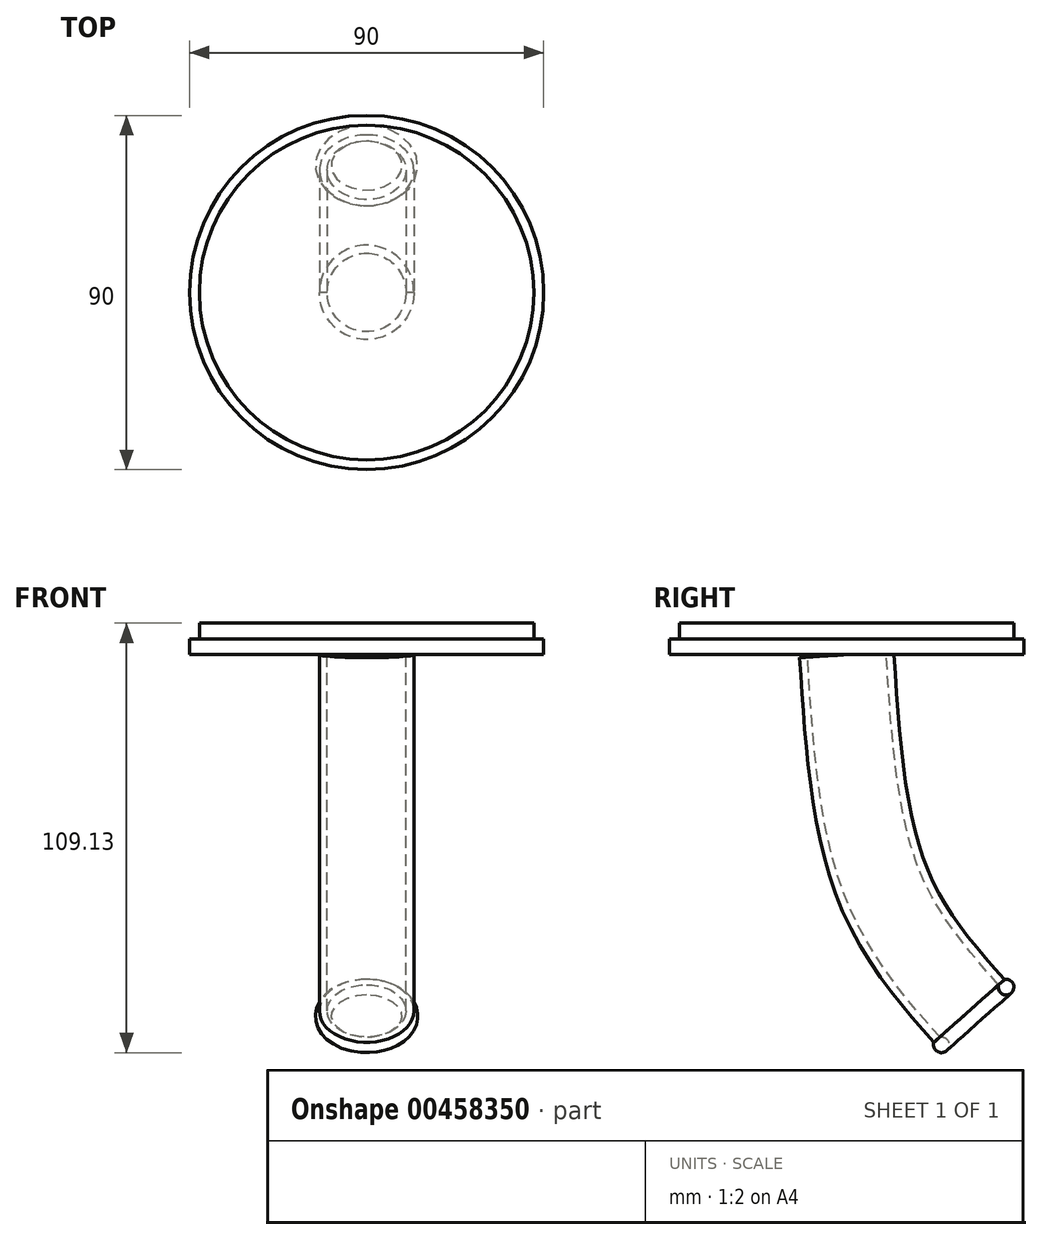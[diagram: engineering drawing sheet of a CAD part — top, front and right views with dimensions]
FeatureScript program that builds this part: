
annotation { "Feature Type Name" : "Feature", "Feature Type Description" : "" }
export const myFeature = defineFeature(function(context is Context, id is Id, definition is map)
    precondition{}
    {
        {
            var Q0;
            Q0=qCreatedBy(makeId("Top.planeOp"),FACE);
            var sketch = newSketch(context, id + "F0", { "sketchPlane" : qUnion([Q0])});
            skCircle(sketch, "E0", {"center": v(0, 0) * mm, "radius": 45 * mm});
            skCircle(sketch, "E1", {"center": v(0, 0) * mm, "radius": 42.5 * mm});
            skSolve(sketch);
        }
        {
            var Q0;
            Q0=makeQuery(id+"F0.imprint","IMPRINT",FACE,{"disambiguationData":[TD([[makeQuery(id+"F0.imprint","IMPRINT",EDGE,{"derivedFrom":sQuery(id+"F0.wireOp",EDGE,"E0")}),1.0]])]});
            extrude(context, id + "F1", {"entities" : qUnion([Q0]), "depth" : 4 * mm});
        }
        {
            var Q0;
            Q0=makeQuery(id+"F0.imprint","IMPRINT",FACE,{"disambiguationData":[TD([[makeQuery(id+"F0.imprint","IMPRINT",EDGE,{"derivedFrom":sQuery(id+"F0.wireOp",EDGE,"E1")}),1.0]])]});
            extrude(context, id + "F2", {"entities" : qUnion([Q0]), "operationType" : NewBodyOperationType.ADD, "depth" : 8 * mm});
        }
        {
            var Q0;
            Q0=qCreatedBy(makeId("Right.planeOp"),FACE);
            var sketch = newSketch(context, id + "F3", { "sketchPlane" : qUnion([Q0])});
            skPoint(sketch, "E2.0", {"position": v(0, 0) * mm});
            skLineSegment(sketch, "E3.0", {"start": v(-45, 0) * mm, "end": v(45, 0) * mm});
            skFitSpline(sketch, "E4", {"points": [v(0, 0) * mm, v(9.12, -58.46) * mm, v(32.23, -91.82) * mm], "startDerivative": vector(7.27, -115.98) * mm, "endDerivative": vector(58.82, -66.1) * mm});
            skSolve(sketch);
        }
        {
            var Q0;
            Q0=sQuery(id+"F3.wireOp",EDGE,"E4");
            var Q1;
            Q1=sQuery(id+"F3.wireOp",VERTEX,"E4.2.internal");
            cPlane(context, id + "F4", {"entities" : qUnion([Q0, Q1]), "cplaneType" : CPlaneType.CURVE_POINT, "offset" : 25.4 * mm, "width" : 152.4 * mm, "height" : 152.4 * mm});
        }
        {
            var Q0;
            Q0=qCreatedBy(id+"F4.planeOp",FACE);
            var sketch = newSketch(context, id + "F5", { "sketchPlane" : qUnion([Q0])});
            skPoint(sketch, "E5.0", {"position": v(0, 36.96) * mm});
            skCircle(sketch, "E6", {"center": v(0, 36.96) * mm, "radius": 10 * mm});
            skCircle(sketch, "E7", {"center": v(0, 36.96) * mm, "radius": 12 * mm});
            skCircle(sketch, "E8", {"center": v(0, 36.96) * mm, "radius": 11 * mm});
            skCircle(sketch, "E9", {"center": v(0, 36.96) * mm, "radius": 13 * mm});
            skPoint(sketch, "E10", {"position": v(2.35, 26.21) * mm});
            skSolve(sketch);
        }
        {
            var Q0;
            Q0=sQuery(id+"F5.wireOp",VERTEX,"E10");
            var Q1;
            Q1=sQuery(id+"F5.wireOp",EDGE,"E8");
            cPlane(context, id + "F6", {"entities" : qUnion([Q0, Q1]), "cplaneType" : CPlaneType.CURVE_POINT, "offset" : 25.4 * mm, "width" : 152.4 * mm, "height" : 152.4 * mm});
        }
        {
            var Q0;
            Q0=qCreatedBy(id+"F6.planeOp",FACE);
            var sketch = newSketch(context, id + "F7", { "sketchPlane" : qUnion([Q0])});
            skPoint(sketch, "E11.0", {"position": v(42.06, -83.45) * mm});
            skLineSegment(sketch, "E12.0", {"start": v(43.54, -82.1) * mm, "end": v(24.32, -99.62) * mm});
            skCircle(sketch, "E13", {"center": v(42.06, -83.45) * mm, "radius": 2 * mm});
            skSolve(sketch);
        }
        {
            var Q0;
            {var subQ0=sQuery(id+"F7.wireOp",EDGE,"E13");var subQ1=sQuery(id+"F7.wireOp",EDGE,"E12.0");var subQ2=makeQuery(id+"F7.imprint","INTERSECT",VERTEX,{"disambiguationData":[OD(0.0)],"derivedFrom":[subQ1,subQ0]});Q0=makeQuery(id+"F7.imprint","IMPRINT",FACE,{"disambiguationData":[TD([[makeQuery(id+"F7.imprint","IMPRINT",EDGE,{"disambiguationData":[TD([[subQ2,-1.0]])],"derivedFrom":subQ1}),1.0]])]});}
            var Q1;
            {var subQ0=sQuery(id+"F7.wireOp",EDGE,"E13");var subQ1=sQuery(id+"F7.wireOp",EDGE,"E12.0");var subQ2=makeQuery(id+"F7.imprint","INTERSECT",VERTEX,{"disambiguationData":[OD(0.0)],"derivedFrom":[subQ1,subQ0]});Q1=makeQuery(id+"F7.imprint","IMPRINT",FACE,{"disambiguationData":[TD([[makeQuery(id+"F7.imprint","IMPRINT",EDGE,{"disambiguationData":[TD([[subQ2,-1.0]])],"derivedFrom":subQ1}),-1.0]])]});}
            var Q2;
            Q2=sQuery(id+"F5.wireOp",EDGE,"E8");
            sweep(context, id + "F8", {"profiles" : qUnion([Q0, Q1]), "path" : qUnion([Q2])});
        }
        {
            var Q0;
            Q0=makeQuery(id+"F5.imprint","IMPRINT",FACE,{"disambiguationData":[TD([[makeQuery(id+"F5.imprint","IMPRINT",EDGE,{"derivedFrom":sQuery(id+"F5.wireOp",EDGE,"E7")}),1.0]])]});
            var Q1;
            Q1=makeQuery(id+"F5.imprint","IMPRINT",FACE,{"disambiguationData":[TD([[makeQuery(id+"F5.imprint","IMPRINT",EDGE,{"derivedFrom":sQuery(id+"F5.wireOp",EDGE,"E6")}),-1.0]])]});
            var Q2;
            Q2=sQuery(id+"F3.wireOp",EDGE,"E4");
            sweep(context, id + "F9", {"operationType" : NewBodyOperationType.ADD, "profiles" : qUnion([Q0, Q1]), "path" : qUnion([Q2])});
        }
    });
